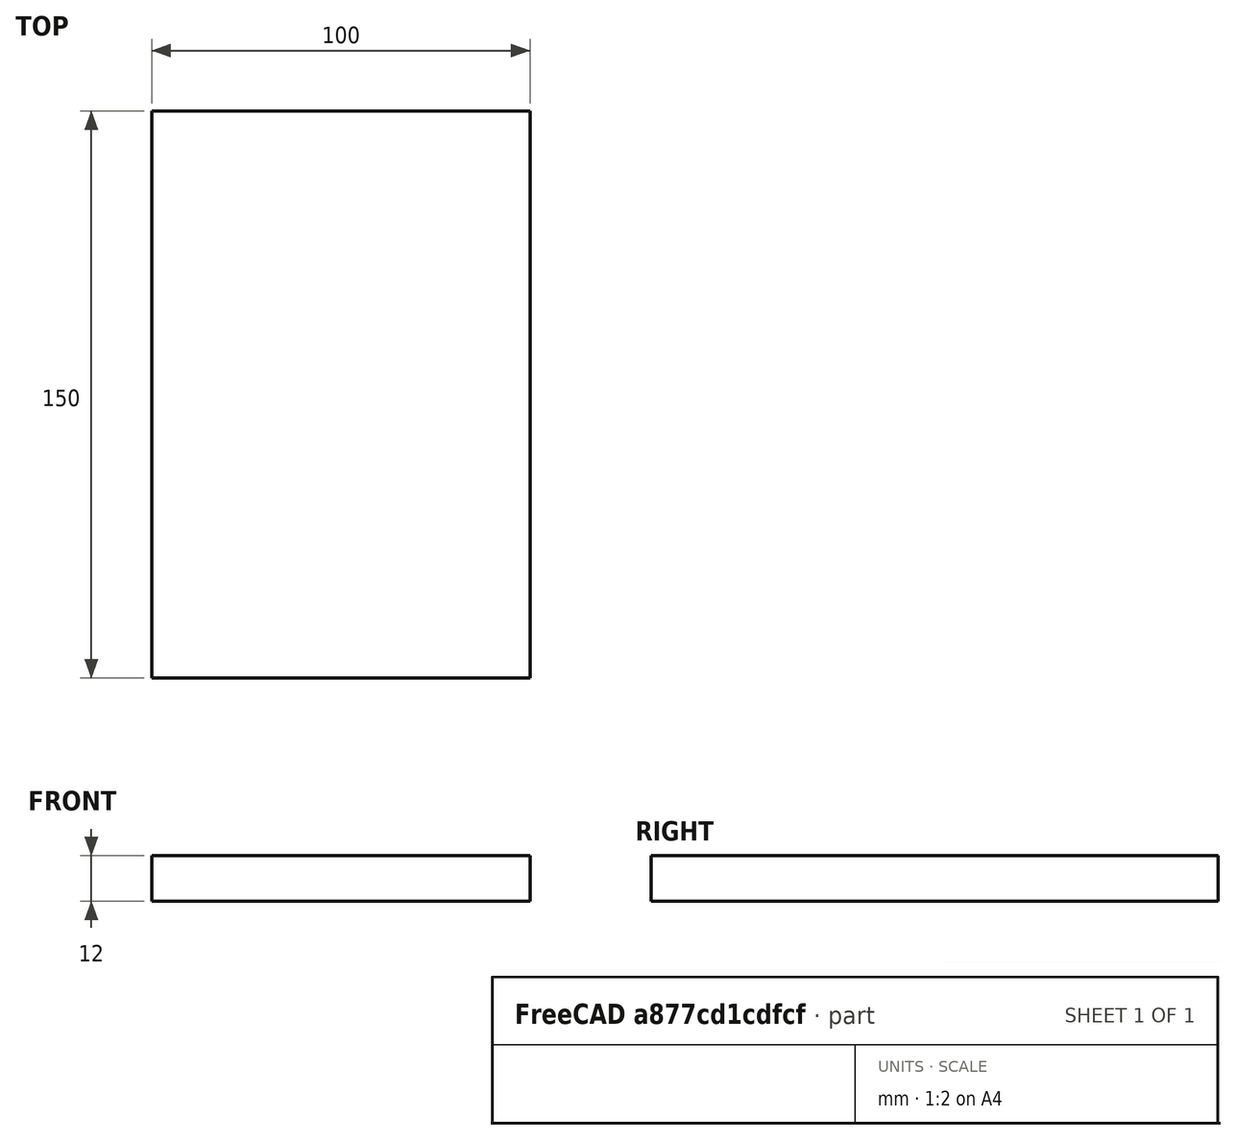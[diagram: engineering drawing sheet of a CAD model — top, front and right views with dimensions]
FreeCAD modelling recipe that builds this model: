
FCSTD DOCUMENT  (FreeCAD 0.16R6703 (Git))
Label: box2_topbottom
License: All rights reserved
LicenseURL: http://en.wikipedia.org/wiki/All_rights_reserved
objects: Drawing::FeatureViewPython×3, Drawing::FeatureViewPart×2, Sketcher::SketchObject×1, PartDesign::Pad×1, Drawing::FeaturePage×1
note: 3 computed .brp shape members not serialized (recipe doc carries the construction recipe); baked Part::Feature solids carry a one-line shape summary decoded from their .brp

FEATURE [Sketcher::SketchObject] Sketch
  sketch-geometry (4):
    g0: LineSegment StartX=-8.38615 StartY=-59.6606 StartZ=0 EndX=91.6138 EndY=-59.6606 EndZ=0
    g1: LineSegment StartX=91.6138 StartY=-59.6606 StartZ=0 EndX=91.6138 EndY=90.3394 EndZ=0
    g2: LineSegment StartX=91.6138 StartY=90.3394 StartZ=0 EndX=-8.38615 EndY=90.3394 EndZ=0
    g3: LineSegment StartX=-8.38615 StartY=90.3394 StartZ=0 EndX=-8.38615 EndY=-59.6606 EndZ=0
  constraints (10):
    c: Coincident(g0,g1)
    c: Coincident(g1,g2)
    c: Coincident(g2,g3)
    c: Coincident(g3,g0)
    c: Horizontal(g0)
    c: Horizontal(g2)
    c: Vertical(g1)
    c: Vertical(g3)
    c: Distance(g0) = 100
    c: Distance(g3) = 150
FEATURE [PartDesign::Pad] Pad
  Length = 12
  Length2 = 100
  Sketch = -> Sketch
  Type = 0
FEATURE [Drawing::FeatureViewPart] Ortho  label="Ortho_0_0"
  Direction = (1,0,0)
  HiddenWidth = 0.15
  LineWidth = 0.35
  Rotation = -90
  Scale = 1.5
  ShowHiddenLines = false
  ShowSmoothLines = false
  Source = -> Pad
  Tolerance = 0.05
  ViewResult = <g id="Ortho_0_0"\n   transform="rotate(-90,186.991,44.3333) translate(186.991,44.3333) scale(1.5,1.5)"\n  >\n<g   stroke="rgb(0, 0, 0)"\n   stroke-width="0.233333"\n   stroke-linecap="butt"\n   stroke-linejoin="miter"\n   fill="none"\n   transform="scale(1,-1)"\n  >\n<path id= "1" d=" M 0 59.6606 L 12 59.6606 " />\n<path id= "2" d=" M 0 -90.3394 L 12 -90.3394 " />\n<path id= "3" d=" M 0 59.6606 L 0 -90.3394 " />\n<path id= "4" d=" M 12 59.6606 L 12 -90.3394 " />\n</g>\n</g>
  Visible = true
  X = 186.991
  Y = 44.3333
FEATURE [Drawing::FeatureViewPart] Ortho001  label="Ortho_0_-1"
  Direction = (0,0,-1)
  HiddenWidth = 0.15
  LineWidth = 0.35
  Rotation = 90
  Scale = 1.5
  ShowHiddenLines = false
  ShowSmoothLines = false
  Source = -> Pad
  Tolerance = 0.05
  ViewResult = <g id="Ortho_0_-1"\n   transform="rotate(90,186.991,198.087) translate(186.991,198.087) scale(1.5,1.5)"\n  >\n<g   stroke="rgb(0, 0, 0)"\n   stroke-width="0.233333"\n   stroke-linecap="butt"\n   stroke-linejoin="miter"\n   fill="none"\n   transform="scale(1,-1)"\n  >\n<path id= "1" d=" M 8.38615 -59.6606 L -91.6138 -59.6606 " />\n<path id= "2" d=" M -91.6138 -59.6606 L -91.6138 90.3394 " />\n<path id= "3" d=" M -91.6138 90.3394 L 8.38615 90.3394 " />\n<path id= "4" d=" M 8.38615 90.3394 L 8.38615 -59.6606 " />\n</g>\n</g>
  Visible = true
  X = 186.991
  Y = 198.087
FEATURE [Drawing::FeatureViewPython] dim001  # drawing view (typed FeaturePython)
  Rotation = 0
  ViewResult = <g> \n  <line x1="95.500100" y1="210.666225" x2="77.925905" y2="210.666225" style="stroke:rgb(0,0,255);stroke-width:0.50" />\n<line x1="95.500100" y1="60.666300" x2="77.925905" y2="60.666300" style="stroke:rgb(0,0,255);stroke-width:0.50" />\n<line x1="78.925905" y1="210.666225" x2="78.925905" y2="60.666300" style="stroke:rgb(0,0,255);stroke-width:0.50" /> \n  <polygon points="78.925905,60.666300 77.925905,63.666300 78.925905,64.666300 79.925905,63.666300" style="fill:rgb(0,0,255);stroke:rgb(0,0,255);stroke-width:0" /><polygon points="78.925905,210.666225 79.925905,207.666225 78.925905,206.666225 77.925905,207.666225" style="fill:rgb(0,0,255);stroke:rgb(0,0,255);stroke-width:0" /> \n  <text x="76.925905" y="135.666262" font-family="inherit" font-size="7" fill="rgb(0,0,255)" text-anchor="middle" transform="rotate(-90.000000 76.925905,135.666262)" >100</text> </g>
  Visible = true
  X = 0
  Y = 0
  arrowL1 = 3
  arrowL2 = 1
  arrowW = 2
  arrow_scheme = 0
  autoPlaceOffset = 2
  autoPlaceText = true
  click1_x = 78.9259
  click1_y = 89.5916
  click2_x = 78.9259
  click2_y = 89.5916
  comma_decimal_place = false
  dimension_line_overshoot = 1
  gap_datum_points = 2
  halfDimension_linear = false
  lineColor = rgb(0,0,255)
  strokeWidth = 0.5
  textFormat_linear = %(value)3.3f
  textRenderer_color = rgb(0,0,255)
  textRenderer_family = inherit
  textRenderer_size = 7
  unit_custom_scale = 0.8
  unit_scheme = 0
FEATURE [Drawing::FeatureViewPython] dim002  # drawing view (typed FeaturePython)
  Rotation = 0
  ViewResult = <g> \n  <line x1="95.500100" y1="44.333300" x2="76.859339" y2="44.333300" style="stroke:rgb(0,0,255);stroke-width:0.50" />\n<line x1="95.500100" y1="26.333300" x2="76.859339" y2="26.333300" style="stroke:rgb(0,0,255);stroke-width:0.50" />\n<line x1="77.859339" y1="44.333300" x2="77.859339" y2="26.333300" style="stroke:rgb(0,0,255);stroke-width:0.50" /> \n  <polygon points="77.859339,26.333300 76.859339,29.333300 77.859339,30.333300 78.859339,29.333300" style="fill:rgb(0,0,255);stroke:rgb(0,0,255);stroke-width:0" /><polygon points="77.859339,44.333300 78.859339,41.333300 77.859339,40.333300 76.859339,41.333300" style="fill:rgb(0,0,255);stroke:rgb(0,0,255);stroke-width:0" /> \n  <text x="75.859339" y="35.333300" font-family="inherit" font-size="7" fill="rgb(0,0,255)" text-anchor="middle" transform="rotate(-90.000000 75.859339,35.333300)" >12</text> </g>
  Visible = true
  X = 0
  Y = 0
  arrowL1 = 3
  arrowL2 = 1
  arrowW = 2
  arrow_scheme = 0
  autoPlaceOffset = 2
  autoPlaceText = true
  click1_x = 77.8593
  click1_y = 40.885
  click2_x = 77.8593
  click2_y = 40.885
  comma_decimal_place = false
  dimension_line_overshoot = 1
  gap_datum_points = 2
  halfDimension_linear = false
  lineColor = rgb(0,0,255)
  strokeWidth = 0.5
  textFormat_linear = %(value)3.3f
  textRenderer_color = rgb(0,0,255)
  textRenderer_family = inherit
  textRenderer_size = 7
  unit_custom_scale = 0.8
  unit_scheme = 0
FEATURE [Drawing::FeatureViewPython] dim003  # drawing view (typed FeaturePython)
  Rotation = 0
  ViewResult = <g> \n  <line x1="322.500100" y1="212.666225" x2="322.500100" y2="223.556831" style="stroke:rgb(0,0,255);stroke-width:0.50" />\n<line x1="97.500100" y1="212.666225" x2="97.500100" y2="223.556831" style="stroke:rgb(0,0,255);stroke-width:0.50" />\n<line x1="322.500100" y1="222.556831" x2="97.500100" y2="222.556831" style="stroke:rgb(0,0,255);stroke-width:0.50" /> \n  <polygon points="97.500100,222.556831 100.500100,223.556831 101.500100,222.556831 100.500100,221.556831" style="fill:rgb(0,0,255);stroke:rgb(0,0,255);stroke-width:0" /><polygon points="322.500100,222.556831 319.500100,221.556831 318.500100,222.556831 319.500100,223.556831" style="fill:rgb(0,0,255);stroke:rgb(0,0,255);stroke-width:0" /> \n  <text x="210.000100" y="220.556831" font-family="inherit" font-size="7" fill="rgb(0,0,255)" text-anchor="middle" transform="rotate(0.000000 210.000100,220.556831)" >150</text> </g>
  Visible = true
  X = 0
  Y = 0
  arrowL1 = 3
  arrowL2 = 1
  arrowW = 2
  arrow_scheme = 0
  autoPlaceOffset = 2
  autoPlaceText = true
  click1_x = 125.144
  click1_y = 222.557
  click2_x = 125.144
  click2_y = 222.557
  comma_decimal_place = false
  dimension_line_overshoot = 1
  gap_datum_points = 2
  halfDimension_linear = false
  lineColor = rgb(0,0,255)
  strokeWidth = 0.5
  textFormat_linear = %(value)3.3f
  textRenderer_color = rgb(0,0,255)
  textRenderer_family = inherit
  textRenderer_size = 7
  unit_custom_scale = 0.8
  unit_scheme = 0
FEATURE [Drawing::FeaturePage] Page
  EditableTexts = AUTHOR NAME | CREATION DATE | SUPERVISOR NAME | CHECK DATE | SCALE | WEIGHT | NUMBER | SHEET | Box 2 Top/Bottom | SUBTITLE
  Group = -> [Ortho,Ortho001,dim001,dim002,dim003]
